# Revit family: 0047831 Feilo Sylvania Lighting Fixture START FLOOD LED 850LM 10W 4000K
name_source: partatom
category: Lighting Fixtures
revit_build: Autodesk Revit 2017 (Build: 20190507_1515(x64)
units: mm (PartAtom-declared; Revit-internal decimal feet)

## family parameters
Cut with Voids When Loaded = No
Host = Face
Light Source = No
OmniClass Number = 23.80.70.00
OmniClass Title = Lighting
Part Type = Normal
Room Calculation Point = No
Round Connector Dimension = Use Diameter
Shared = No

## types (1)
- 0047831 START FLOOD LED 850LM 10W 4000K
    Apparent Load = 10 VA
    Assembly Code = D5020200
    AssetType = Fixed
    BracketAxisFromTop_FEILO = 9 mm  [stored 0.0295276 ft]
    BracketFillet_FEILO = 8 mm  [stored 0.0262467 ft]
    BracketHeight_FEILO = 82 mm  [stored 0.269029 ft]
    BracketInnerWidth_FEILO = 103 mm  [stored 0.337927 ft]
    BracketRadiusOuter_FEILO = 12 mm  [stored 0.0393701 ft]
    BracketRadius_FEILO = 10 mm  [stored 0.0328084 ft]
    BracketThickness_FEILO = 2 mm  [stored 0.00656168 ft]
    BracketWidth_FEILO = 18 mm  [stored 0.0590551 ft]
    ClassificationName = Uniclass2015
    ClassificationValue = EF_70_80
    Cost = 0 $
    Default Elevation = 1219 mm
    Description = LED IP65 floodlight, 850LM, 10W, 4000K, 100 degree beam angle, black aluminium die-cast body, slimline 49.3mmx113mmx122mm, lifetime 30,000hrs.
    DocumentationLiterature = http://www.sylvania-lighting.com
    DurationUnit = hours
    ElectricShockClassification = Class I
    ExpectedLife = 50000
    IfcExportAs = IfcLightFixtureType
    IfcExportType = IfcLightFixtureType
    ImpactProtectionIndex = IK07
    IngressProtection = IP65
    InputVoltage = 220-240V~
    Keynote = 16500
    Lamp = LED
    LampColourRenderingIndex = 0
    LampColourTemperature = 4000 K
    LampNominalLuminous = 850 lm
    LampsType = LED
    LightOutputRatio = 100
    LuminousEfficacy = 85 lm/W
    Manufacturer = Feilo Sylvania
    ManufacturerName = Feilo Sylvania
    Material = die-cast aluminium housing, glass diffuser
    Material_1_FEILO = Body-Sylvania-StartFlood-Black
    Material_2_FEILO = <By Category>
    Material_3_FEILO = <By Category>
    Material_4_FEILO = <By Category>
    Model = START FLOOD LED 850LM 10W 4000K
    ModelNumber = 0047831
    ModelReference = START FLOOD LED 850LM 10W 4000K
    Name = START FLOOD LED 850LM 10W 4000K
    NominalDepth = 122 mm  [stored 0.400262 ft]
    NominalHeight = 149 mm
    NominalLength = 49 mm
    PowerConsumption = 10 W
    PowerFactor = 0
    Type Image = <None>
    TypeName = START FLOOD LED 850LM 10W 4000K
    URL = http://www.sylvania-lighting.com
    Voltage = 230 V
    Weight = 2.718 kg

note: [stored X ft] marks values corroborated as IEEE doubles in the binary element streams (Revit-internal decimal feet)

## geometry (parser evidence)
native form markers: Sweep x4
no freeform markers — native parametric forms only
